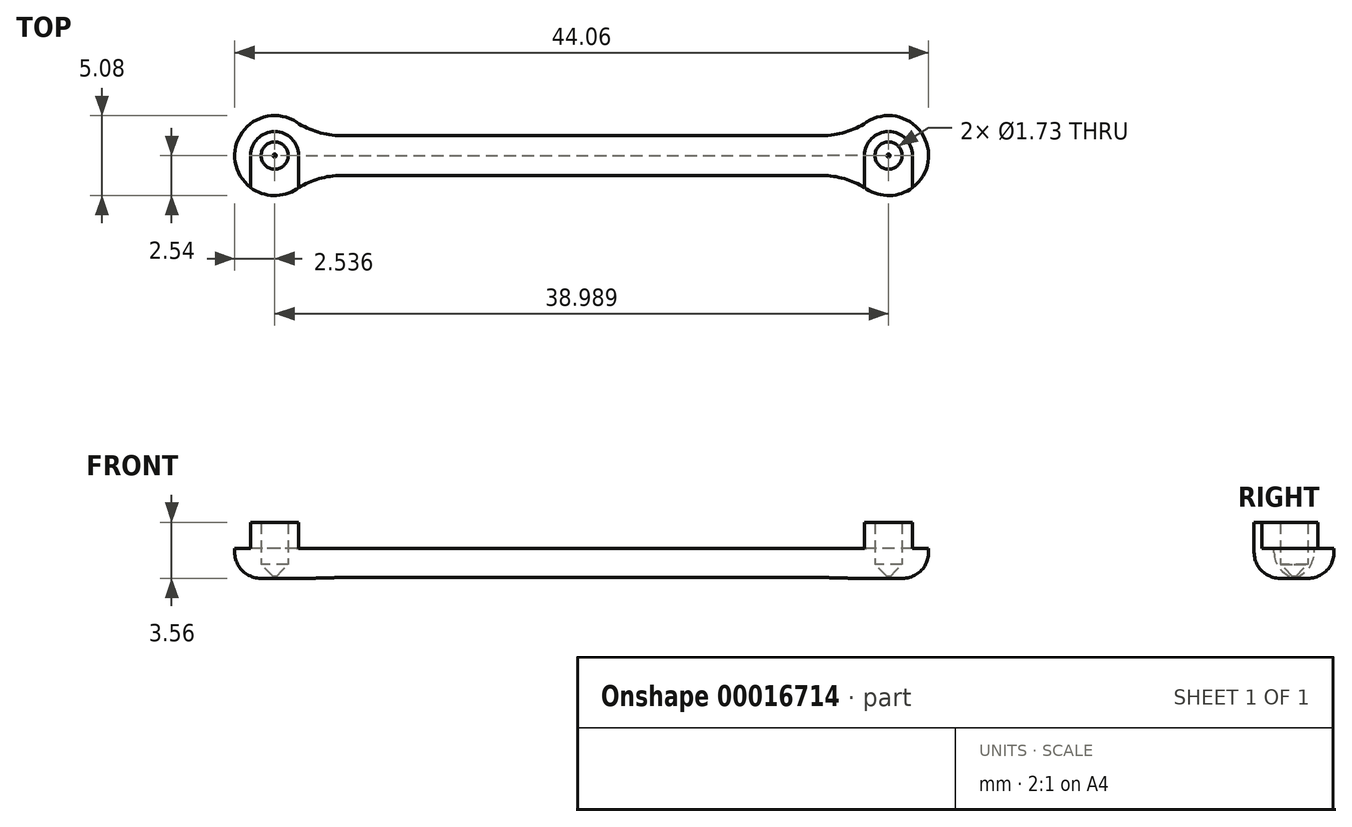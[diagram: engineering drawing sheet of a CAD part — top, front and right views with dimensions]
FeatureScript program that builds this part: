
annotation { "Feature Type Name" : "Feature", "Feature Type Description" : "" }
export const myFeature = defineFeature(function(context is Context, id is Id, definition is map)
    precondition{}
    {
        {
            var Q0;
            Q0=qCreatedBy(makeId("Top.planeOp"),FACE);
            var sketch = newSketch(context, id + "F0", { "sketchPlane" : qUnion([Q0])});
            skLineSegment(sketch, "E0.rect.top", {"start": v(-17.3, -1.27) * mm, "end": v(17.3, -1.27) * mm});
            skPoint(sketch, "E0.rect.middle", {"position": v(0, 0) * mm});
            skArc(sketch, "E1", {"start": v(-17.3, 1.27) * mm, "mid": v(-22.03, 0) * mm, "end": v(-17.3, -1.27) * mm});
            skArc(sketch, "E2", {"start": v(17.3, -1.27) * mm, "mid": v(22.03, 0) * mm, "end": v(17.3, 1.27) * mm});
            skArc(sketch, "E3", {"start": v(-17.97, 0) * mm, "mid": v(-19.5, 1.52) * mm, "end": v(-21.02, 0) * mm});
            skArc(sketch, "E4", {"start": v(21.02, 0) * mm, "mid": v(19.5, 1.52) * mm, "end": v(17.97, 0) * mm});
            skCircle(sketch, "E5", {"center": v(-19.5, 0) * mm, "radius": 0.86 * mm});
            skCircle(sketch, "E6", {"center": v(19.5, 0) * mm, "radius": 0.86 * mm});
            skLineSegment(sketch, "E7.trimOffspring", {"start": v(-17.3, 1.27) * mm, "end": v(17.3, 1.27) * mm});
            skLineSegment(sketch, "E8", {"start": v(-17.97, 0) * mm, "end": v(-17.97, -2.03) * mm});
            skLineSegment(sketch, "E9", {"start": v(-21.02, 0) * mm, "end": v(-21.02, -2.03) * mm});
            skLineSegment(sketch, "E10", {"start": v(17.97, 0) * mm, "end": v(17.97, -2.03) * mm});
            skLineSegment(sketch, "E11", {"start": v(21.02, 0) * mm, "end": v(21.02, -2.03) * mm});
            skSolve(sketch);
        }
        {
            var Q0;
            Q0 = qSketchRegion(id + "F0", true);
            extrude(context, id + "F1", {"entities" : qUnion([Q0]), "depth" : 1.9 * mm});
        }
        {
            var Q0;
            Q0=makeQuery(id+"F0.imprint","IMPRINT",FACE,{"disambiguationData":[TD([[makeQuery(id+"F0.imprint","IMPRINT",EDGE,{"derivedFrom":sQuery(id+"F0.wireOp",EDGE,"E3")}),1.0]])]});
            var Q1;
            Q1=makeQuery(id+"F0.imprint","IMPRINT",FACE,{"disambiguationData":[TD([[makeQuery(id+"F0.imprint","IMPRINT",EDGE,{"derivedFrom":sQuery(id+"F0.wireOp",EDGE,"E4")}),1.0]])]});
            extrude(context, id + "F2", {"entities" : qUnion([Q0, Q1]), "operationType" : NewBodyOperationType.ADD, "depth" : 3.56 * mm});
        }
        {
            var Q0;
            Q0=makeQuery(id+"F0.imprint","IMPRINT",FACE,{"disambiguationData":[TD([[makeQuery(id+"F0.imprint","IMPRINT",EDGE,{"derivedFrom":sQuery(id+"F0.wireOp",EDGE,"E3")}),1.0]])]});
            var Q1;
            Q1=makeQuery(id+"F0.imprint","IMPRINT",FACE,{"disambiguationData":[TD([[makeQuery(id+"F0.imprint","IMPRINT",EDGE,{"derivedFrom":sQuery(id+"F0.wireOp",EDGE,"E5")}),1.0]])]});
            var Q2;
            Q2=makeQuery(id+"F0.imprint","IMPRINT",FACE,{"disambiguationData":[TD([[makeQuery(id+"F0.imprint","IMPRINT",EDGE,{"derivedFrom":sQuery(id+"F0.wireOp",EDGE,"E4")}),1.0]])]});
            var Q3;
            Q3=makeQuery(id+"F0.imprint","IMPRINT",FACE,{"disambiguationData":[TD([[makeQuery(id+"F0.imprint","IMPRINT",EDGE,{"derivedFrom":sQuery(id+"F0.wireOp",EDGE,"E6")}),1.0]])]});
            extrude(context, id + "F3", {"entities" : qUnion([Q0, Q1, Q2, Q3]), "operationType" : NewBodyOperationType.ADD, "depth" : 0.13 * mm});
        }
        {
            var Q0;
            Q0=makeQuery(id+"F1.opExtrude","SWEPT_EDGE",EDGE,{"disambiguationData":[OSD([sQuery(id+"F0.wireOp",EDGE,"E0.rect.top"),sQuery(id+"F0.wireOp",EDGE,"E1")])]});
            var Q1;
            Q1=makeQuery(id+"F1.opExtrude","SWEPT_EDGE",EDGE,{"disambiguationData":[OSD([sQuery(id+"F0.wireOp",EDGE,"E0.rect.top"),sQuery(id+"F0.wireOp",EDGE,"E2")])]});
            var Q2;
            Q2=makeQuery(id+"F1.opExtrude","SWEPT_EDGE",EDGE,{"disambiguationData":[OSD([sQuery(id+"F0.wireOp",EDGE,"E2"),sQuery(id+"F0.wireOp",EDGE,"E7.trimOffspring")])]});
            var Q3;
            Q3=makeQuery(id+"F1.opExtrude","SWEPT_EDGE",EDGE,{"disambiguationData":[OSD([sQuery(id+"F0.wireOp",EDGE,"E1"),sQuery(id+"F0.wireOp",EDGE,"E7.trimOffspring")])]});
            fillet(context, id + "F4", {"entities" : qUnion([Q0, Q1, Q2, Q3]), "radius" : 5.08 * mm, "tangentPropagation" : true, "allowEdgeOverflow" : false});
        }
        {
            var Q0;
            Q0=makeQuery(id+"F1.opExtrude","CAP_EDGE",EDGE,{"disambiguationData":[OSD([sQuery(id+"F0.wireOp",EDGE,"E7.trimOffspring")])],"isStart":true});
            fillet(context, id + "F5", {"entities" : qUnion([Q0]), "radius" : 1.65 * mm, "tangentPropagation" : true, "allowEdgeOverflow" : false});
        }
        {
            var Q0;
            {var subQ0=sQuery(id+"F0.wireOp",EDGE,"E5");Q0=makeQuery(id+"F3.boolean.opBoolean","INTERSECT",EDGE,{"derivedFrom":[makeQuery(id+"F2.boolean.opBoolean","MERGE",FACE,{"derivedFrom":[makeQuery(id+"F1.opExtrude","SWEPT_FACE",FACE,{"disambiguationData":[OSD([subQ0])]}),makeQuery(id+"F2.opExtrude","SWEPT_FACE",FACE,{"disambiguationData":[OSD([subQ0])]})]}),makeQuery(id+"F3.opExtrude","CAP_FACE",FACE,{"disambiguationData":[OSD([sQuery(id+"F0.wireOp",EDGE,"E1"),sQuery(id+"F0.wireOp",EDGE,"E3"),sQuery(id+"F0.wireOp",EDGE,"E8"),sQuery(id+"F0.wireOp",EDGE,"E9")])],"isStart":false})]});}
            var Q1;
            Q1=makeQuery(id+"F3.opExtrude","CAP_FACE",FACE,{"disambiguationData":[OSD([sQuery(id+"F0.wireOp",EDGE,"E2"),sQuery(id+"F0.wireOp",EDGE,"E4"),sQuery(id+"F0.wireOp",EDGE,"E10"),sQuery(id+"F0.wireOp",EDGE,"E11")])],"isStart":false});
            chamfer(context, id + "F6", {"entities" : qUnion([Q0, Q1]), "width" : 0.76 * mm, "tangentPropagation" : true});
        }
    });
